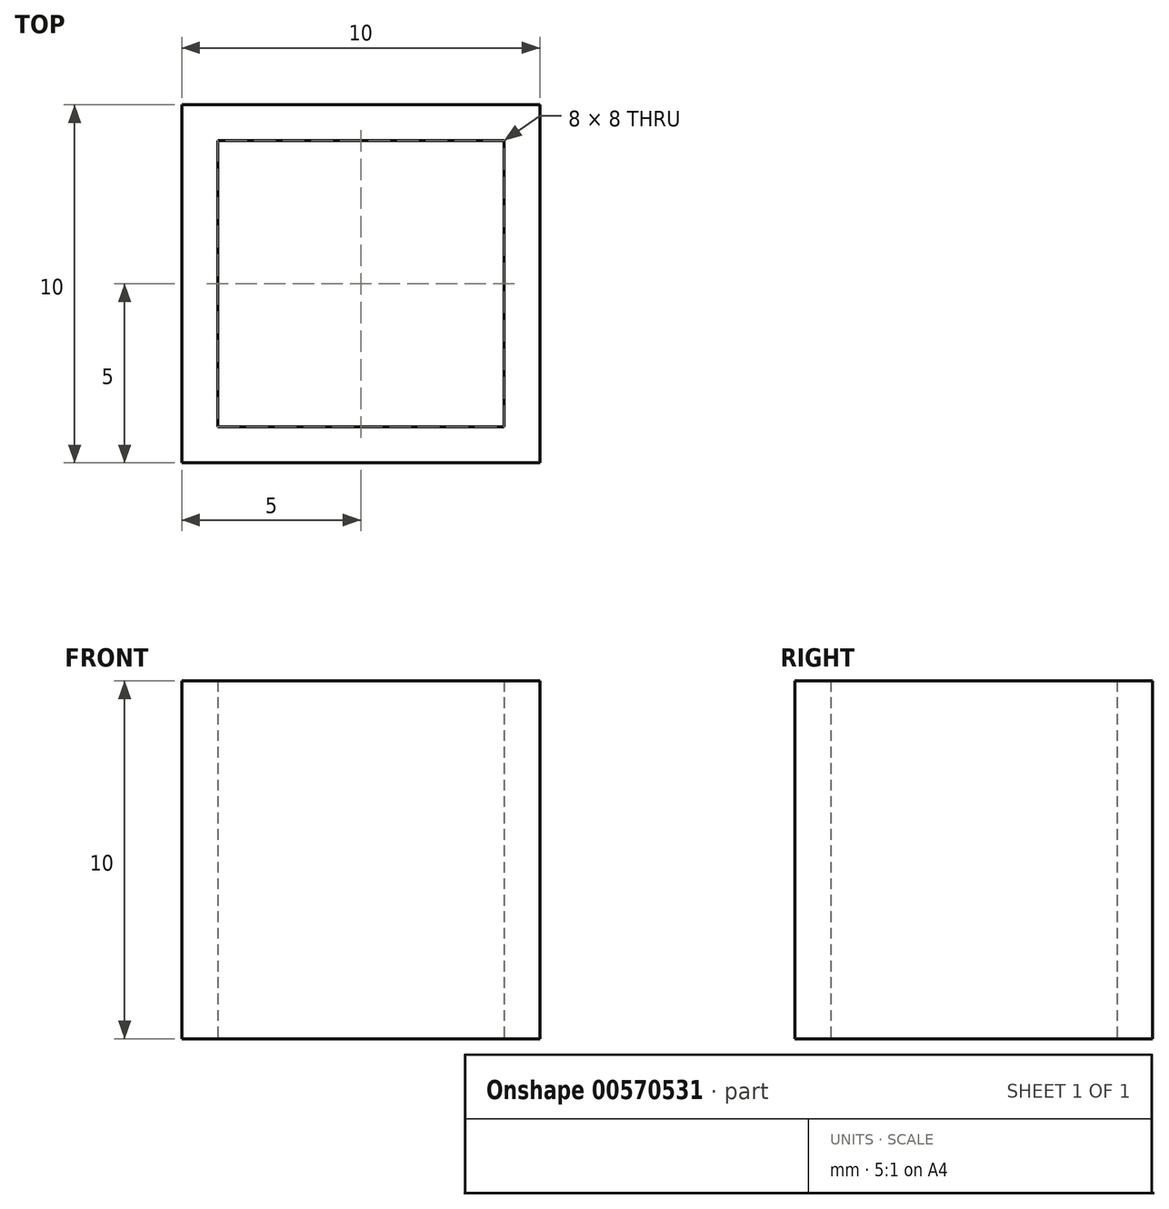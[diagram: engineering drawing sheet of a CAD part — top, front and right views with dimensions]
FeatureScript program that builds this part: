
annotation { "Feature Type Name" : "Feature", "Feature Type Description" : "" }
export const myFeature = defineFeature(function(context is Context, id is Id, definition is map)
    precondition{}
    {
        {
            assignVariable(context, id + "F0", {"name" : "cubeHeight", "anyValue" : 10 * mm});
        }
        {
            var Q0;
            Q0=qCreatedBy(makeId("Top.planeOp"),FACE);
            var sketch = newSketch(context, id + "F1", { "sketchPlane" : qUnion([Q0])});
            skLineSegment(sketch, "E0.bottom", {"start": v(5, -5) * mm, "end": v(-5, -5) * mm});
            skLineSegment(sketch, "E0.top", {"start": v(5, 5) * mm, "end": v(-5, 5) * mm});
            skLineSegment(sketch, "E0.left", {"start": v(5, -5) * mm, "end": v(5, 5) * mm});
            skLineSegment(sketch, "E0.right", {"start": v(-5, -5) * mm, "end": v(-5, 5) * mm});
            skPoint(sketch, "E0.middle", {"position": v(0, 0) * mm});
            skLineSegment(sketch, "E1.0", {"start": v(4, -4) * mm, "end": v(4, 4) * mm});
            skLineSegment(sketch, "E1.1", {"start": v(4, -4) * mm, "end": v(-4, -4) * mm});
            skLineSegment(sketch, "E1.2", {"start": v(-4, -4) * mm, "end": v(-4, 4) * mm});
            skLineSegment(sketch, "E1.3", {"start": v(4, 4) * mm, "end": v(-4, 4) * mm});
            skSolve(sketch);
        }
        {
            var Q0;
            Q0=makeQuery(id+"F1.imprint","IMPRINT",FACE,{"disambiguationData":[TD([[makeQuery(id+"F1.imprint","IMPRINT",EDGE,{"derivedFrom":sQuery(id+"F1.wireOp",EDGE,"E0.bottom")}),-1.0]])]});
            extrude(context, id + "F2", {"entities" : qUnion([Q0]), "depth" : getVariable(context, 'cubeHeight'), "offsetDistance" : 25 * mm});
        }
    });
